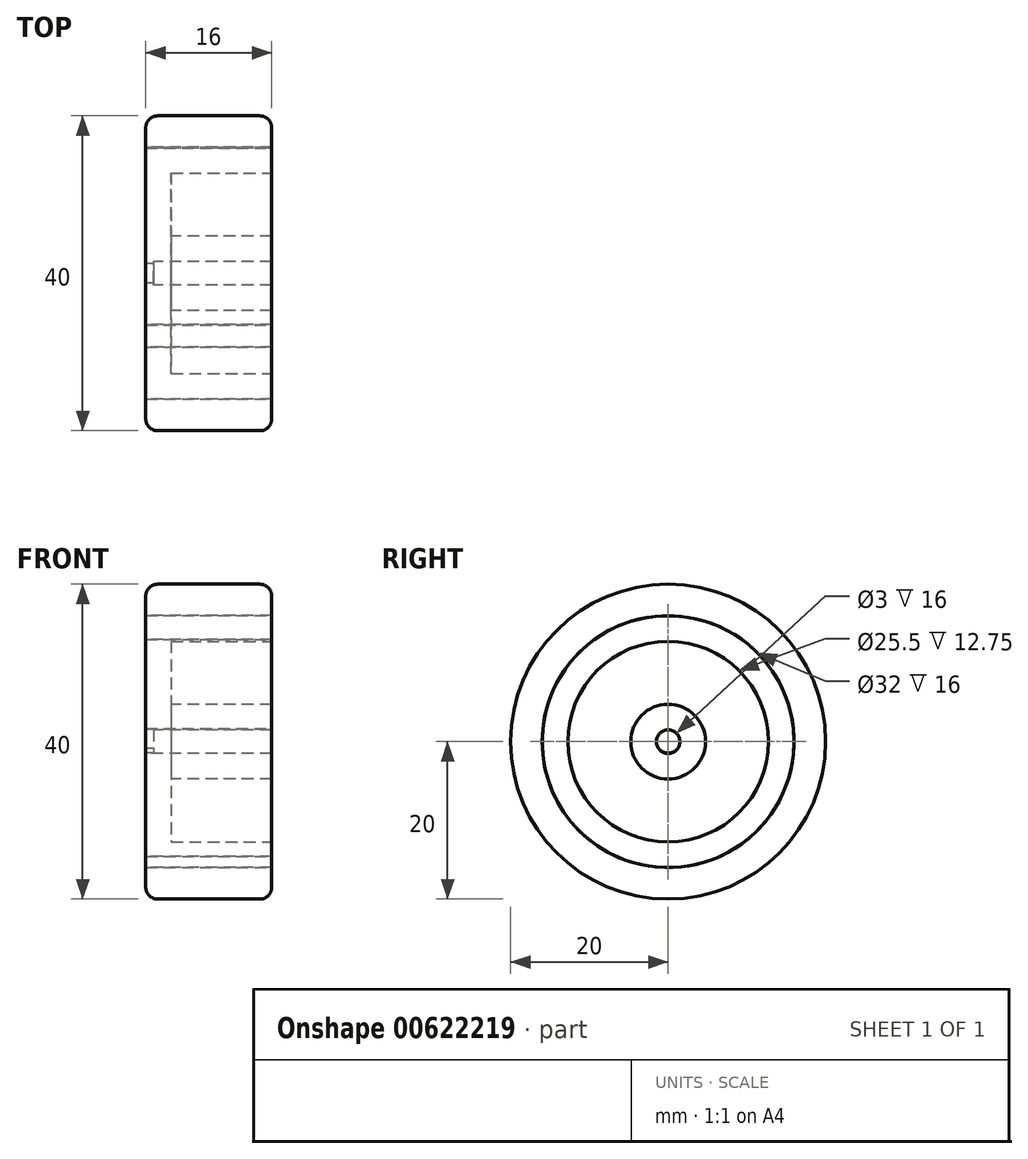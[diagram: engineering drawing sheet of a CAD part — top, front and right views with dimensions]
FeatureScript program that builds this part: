
annotation { "Feature Type Name" : "Feature", "Feature Type Description" : "" }
export const myFeature = defineFeature(function(context is Context, id is Id, definition is map)
    precondition{}
    {
        {
            var Q0;
            Q0=qCreatedBy(makeId("Front.planeOp"),FACE);
            var sketch = newSketch(context, id + "F0", { "sketchPlane" : qUnion([Q0])});
            skLineSegment(sketch, "E0.bottom", {"start": v(0, 0) * mm, "end": v(16, 0) * mm});
            skLineSegment(sketch, "E1.bottom", {"start": v(6, 0) * mm, "end": v(10, 0) * mm});
            skLineSegment(sketch, "E1.top", {"start": v(6, -16) * mm, "end": v(10, -16) * mm});
            skLineSegment(sketch, "E1.left", {"start": v(6, -13) * mm, "end": v(6, -14.5) * mm});
            skLineSegment(sketch, "E1.right", {"start": v(10, -13) * mm, "end": v(10, -14.5) * mm});
            skLineSegment(sketch, "E2.bottom", {"start": v(0, -16) * mm, "end": v(16, -16) * mm, "construction": true});
            skLineSegment(sketch, "E2.top", {"start": v(0, -13) * mm, "end": v(16, -13) * mm});
            skLineSegment(sketch, "E2.left", {"start": v(0, -14.5) * mm, "end": v(0, -13) * mm});
            skLineSegment(sketch, "E3", {"start": v(16, -14.5) * mm, "end": v(0, -14.5) * mm});
            skLineSegment(sketch, "E4", {"start": v(16, -14.5) * mm, "end": v(16, -13) * mm});
            skLineSegment(sketch, "E5.bottom", {"start": v(10, -13) * mm, "end": v(6, -13) * mm});
            skLineSegment(sketch, "E5.top", {"start": v(10, -10.5) * mm, "end": v(6, -10.5) * mm});
            skLineSegment(sketch, "E5.left", {"start": v(10, -13) * mm, "end": v(10, -10.5) * mm});
            skLineSegment(sketch, "E5.right", {"start": v(6, -13) * mm, "end": v(6, -10.5) * mm});
            skArc(sketch, "E6", {"start": v(1.5, 4) * mm, "mid": v(0.44, 3.56) * mm, "end": v(0, 2.5) * mm});
            skLineSegment(sketch, "E7", {"start": v(16, 4.74) * mm, "end": v(14.5, 4.74) * mm});
            skArc(sketch, "E8", {"start": v(16, 2.5) * mm, "mid": v(15.56, 3.56) * mm, "end": v(14.5, 4) * mm});
            skLineSegment(sketch, "E9", {"start": v(0, 2.5) * mm, "end": v(0, 0) * mm});
            skLineSegment(sketch, "E10", {"start": v(16, 0) * mm, "end": v(16, 2.5) * mm});
            skLineSegment(sketch, "E11", {"start": v(14.5, 4) * mm, "end": v(1.5, 4) * mm});
            skPoint(sketch, "E12.end.orphan", {"position": v(8, 0) * mm});
            skPoint(sketch, "E12.start.orphan", {"position": v(8, -10.5) * mm});
            skSolve(sketch);
        }
        {
            var Q0;
            Q0=qSketchRegion(id+"F0",true);
            var Q1;
            Q1=sQuery(id+"F0.wireOp",EDGE,"E1.top");
            revolve(context, id + "F1", {"entities" : qUnion([Q0]), "axis" : qUnion([Q1]), "revolveType" : RevolveType.FULL});
        }
        {
            var Q0;
            Q0=makeQuery(id+"F1.opRevolve","SWEPT_FACE",FACE,{"disambiguationData":[OSD([sQuery(id+"F0.wireOp",EDGE,"E5.right"),sQuery(id+"F0.wireOp",EDGE,"ZnnQBpbw-xC8R-MT8B-JQXv-VcrKk8POS6gG")])]});
            var sketch = newSketch(context, id + "F2", { "sketchPlane" : qUnion([Q0])});
            skLineSegment(sketch, "E13", {"start": v(-2.5, -14.35) * mm, "end": v(-15.91, -14.35) * mm});
            skLineSegment(sketch, "E14.1.1", {"start": v(-0.18, -19) * mm, "end": v(6.53, -30.6) * mm});
            skLineSegment(sketch, "E14.2.1", {"start": v(2.68, -14.65) * mm, "end": v(9.39, -3.04) * mm});
            skPoint(sketch, "E14.center", {"position": v(0, -16) * mm});
            skLineSegment(sketch, "E15", {"start": v(-15.91, -14.35) * mm, "end": v(-15.91, -17.46) * mm});
            skLineSegment(sketch, "E16", {"start": v(-15.91, -17.46) * mm, "end": v(-2.62, -17.46) * mm});
            skLineSegment(sketch, "E17", {"start": v(9.39, -3.04) * mm, "end": v(6.7, -1.49) * mm});
            skLineSegment(sketch, "E18", {"start": v(6.53, -30.6) * mm, "end": v(9.37, -28.97) * mm});
            skPoint(sketch, "E18.endSnap0", {"position": v(9.37, -29.3) * mm});
            skLineSegment(sketch, "E19", {"start": v(9.37, -28.97) * mm, "end": v(2.73, -17.46) * mm});
            skLineSegment(sketch, "E20", {"start": v(6.7, -1.49) * mm, "end": v(0.04, -13) * mm});
            skSolve(sketch);
        }
        {
            var Q0;
            {var subQ0=sQuery(id+"F2.wireOp",EDGE,"E17");Q0=makeQuery(id+"F2.imprint","IMPRINT",FACE,{"disambiguationData":[TD([[makeQuery(id+"F2.imprint","IMPRINT",EDGE,{"derivedFrom":subQ0}),1.0]])]});}
            var Q1;
            {var subQ0=sQuery(id+"F2.wireOp",EDGE,"E18");Q1=makeQuery(id+"F2.imprint","IMPRINT",FACE,{"disambiguationData":[TD([[makeQuery(id+"F2.imprint","IMPRINT",EDGE,{"derivedFrom":subQ0}),1.0]])]});}
            var Q2;
            {var subQ0=sQuery(id+"F2.wireOp",EDGE,"E15");Q2=makeQuery(id+"F2.imprint","IMPRINT",FACE,{"disambiguationData":[TD([[makeQuery(id+"F2.imprint","IMPRINT",EDGE,{"derivedFrom":subQ0}),1.0]])]});}
            extrude(context, id + "F3", {"entities" : qUnion([Q0, Q1, Q2]), "operationType" : NewBodyOperationType.ADD, "oppositeDirection" : true, "depth" : 4 * mm});
        }
        {
            var Q0;
            Q0=qCreatedBy(makeId("Right.planeOp"),FACE);
            var sketch = newSketch(context, id + "F4", { "sketchPlane" : qUnion([Q0])});
            skCircle(sketch, "E21", {"center": v(0, -15.89) * mm, "radius": 1.57 * mm});
            skSolve(sketch);
        }
        {
            var Q0;
            Q0=makeQuery(id+"F4.imprint","IMPRINT",FACE,{"disambiguationData":[TD([[makeQuery(id+"F4.imprint","IMPRINT",EDGE,{"derivedFrom":sQuery(id+"F4.wireOp",EDGE,"E21")}),1.0]])]});
            var Q1;
            Q1=sQuery(id+"F4.wireOp",EDGE,"E21");
            extrude(context, id + "F5", {"entities" : qUnion([Q0]), "operationType" : NewBodyOperationType.ADD, "surfaceEntities" : qUnion([Q1]), "depth" : 1 * mm});
        }
        {
            var Q0;
            Q0=makeQuery(id+"F3.opExtrude","SWEPT_FACE",FACE,{"disambiguationData":[OSD([sQuery(id+"F2.wireOp",EDGE,"E19")])]});
            var Q1;
            Q1=makeQuery(id+"F1.opRevolve","SWEPT_EDGE",EDGE,{"disambiguationData":[OSD([sQuery(id+"F0.wireOp",EDGE,"E3"),sQuery(id+"F0.wireOp",EDGE,"E4")])]});
            revolve(context, id + "F6", {"operationType" : NewBodyOperationType.ADD, "entities" : qUnion([Q0]), "axis" : qUnion([Q1]), "revolveType" : RevolveType.FULL});
        }
        {
            var Q0;
            {var subQ0=sQuery(id+"F2.wireOp",EDGE,"E19");var subQ1=sQuery(id+"F0.wireOp",EDGE,"E5.right");var subQ2=sQuery(id+"F0.wireOp",EDGE,"E5.top");Q0=makeQuery(id+"F6.boolean.opBoolean","MERGE",FACE,{"derivedFrom":[makeQuery(id+"F3.boolean.opBoolean","MERGE",FACE,{"derivedFrom":[makeQuery(id+"F1.opRevolve","SWEPT_FACE",FACE,{"disambiguationData":[OSD([sQuery(id+"F0.wireOp",EDGE,"E5.left")])]}),makeQuery(id+"F3.opExtrude","CAP_FACE",FACE,{"disambiguationData":[OSD([subQ2,subQ1,sQuery(id+"F2.wireOp",EDGE,"E13"),sQuery(id+"F2.wireOp",EDGE,"E15"),sQuery(id+"F2.wireOp",EDGE,"E16")])],"isStart":false}),makeQuery(id+"F3.opExtrude","CAP_FACE",FACE,{"disambiguationData":[OSD([subQ2,subQ1,sQuery(id+"F2.wireOp",EDGE,"E14.1.1"),sQuery(id+"F2.wireOp",EDGE,"E18"),subQ0])],"isStart":false}),makeQuery(id+"F3.opExtrude","CAP_FACE",FACE,{"disambiguationData":[OSD([subQ2,subQ1,sQuery(id+"F2.wireOp",EDGE,"E14.2.1"),sQuery(id+"F2.wireOp",EDGE,"E17"),sQuery(id+"F2.wireOp",EDGE,"E20")])],"isStart":false})]}),makeQuery(id+"F6.opRevolve","SWEPT_FACE",FACE,{"disambiguationData":[OSD([subQ0]),TDD([makeQuery(id+"F3.opExtrude","CAP_EDGE",EDGE,{"disambiguationData":[OSD([subQ0])],"isStart":false})])]})]});}
            extrude(context, id + "F7", {"entities" : qUnion([Q0]), "operationType" : NewBodyOperationType.ADD, "depth" : 6 * mm, "offsetDistance" : 25 * mm});
        }
        {
            var Q0;
            {var subQ0=sQuery(id+"F2.wireOp",EDGE,"E19");var subQ1=sQuery(id+"F0.wireOp",EDGE,"E5.right");var subQ2=sQuery(id+"F0.wireOp",EDGE,"E5.top");Q0=makeQuery(id+"F6.boolean.opBoolean","MERGE",FACE,{"derivedFrom":[makeQuery(id+"F3.boolean.opBoolean","MERGE",FACE,{"derivedFrom":[makeQuery(id+"F1.opRevolve","SWEPT_FACE",FACE,{"disambiguationData":[OSD([subQ1])]}),makeQuery(id+"F3.opExtrude","CAP_FACE",FACE,{"disambiguationData":[OSD([subQ2,subQ1,sQuery(id+"F2.wireOp",EDGE,"E13"),sQuery(id+"F2.wireOp",EDGE,"E15"),sQuery(id+"F2.wireOp",EDGE,"E16")])],"isStart":true}),makeQuery(id+"F3.opExtrude","CAP_FACE",FACE,{"disambiguationData":[OSD([subQ2,subQ1,sQuery(id+"F2.wireOp",EDGE,"E14.1.1"),sQuery(id+"F2.wireOp",EDGE,"E18"),subQ0])],"isStart":true}),makeQuery(id+"F3.opExtrude","CAP_FACE",FACE,{"disambiguationData":[OSD([subQ2,subQ1,sQuery(id+"F2.wireOp",EDGE,"E14.2.1"),sQuery(id+"F2.wireOp",EDGE,"E17"),sQuery(id+"F2.wireOp",EDGE,"E20")])],"isStart":true})]}),makeQuery(id+"F6.opRevolve","SWEPT_FACE",FACE,{"disambiguationData":[OSD([subQ0]),TDD([makeQuery(id+"F3.opExtrude","CAP_EDGE",EDGE,{"disambiguationData":[OSD([subQ0])],"isStart":true})])]})]});}
            extrude(context, id + "F8", {"entities" : qUnion([Q0]), "operationType" : NewBodyOperationType.ADD, "depth" : 6 * mm, "offsetDistance" : 25 * mm});
        }
        {
            var Q0;
            Q0=makeQuery(id+"F7.boolean.opBoolean","MERGE",FACE,{"derivedFrom":[makeQuery(id+"F1.opRevolve","SWEPT_FACE",FACE,{"disambiguationData":[OSD([sQuery(id+"F0.wireOp",EDGE,"E4")])]}),makeQuery(id+"F7.opExtrude","CAP_FACE",FACE,{"disambiguationData":[OSD([sQuery(id+"F0.wireOp",EDGE,"E5.top"),sQuery(id+"F0.wireOp",EDGE,"E5.left"),sQuery(id+"F0.wireOp",EDGE,"E5.right"),sQuery(id+"F2.wireOp",EDGE,"E13"),sQuery(id+"F2.wireOp",EDGE,"E14.1.1"),sQuery(id+"F2.wireOp",EDGE,"E14.2.1"),sQuery(id+"F2.wireOp",EDGE,"E15"),sQuery(id+"F2.wireOp",EDGE,"E16"),sQuery(id+"F2.wireOp",EDGE,"E18"),sQuery(id+"F2.wireOp",EDGE,"E19"),sQuery(id+"F2.wireOp",EDGE,"E17"),sQuery(id+"F2.wireOp",EDGE,"E20")])],"isStart":false})]});
            shell(context, id + "F9", {"entities" : qUnion([Q0]), "thickness" : 3.25 * mm});
        }
    });
